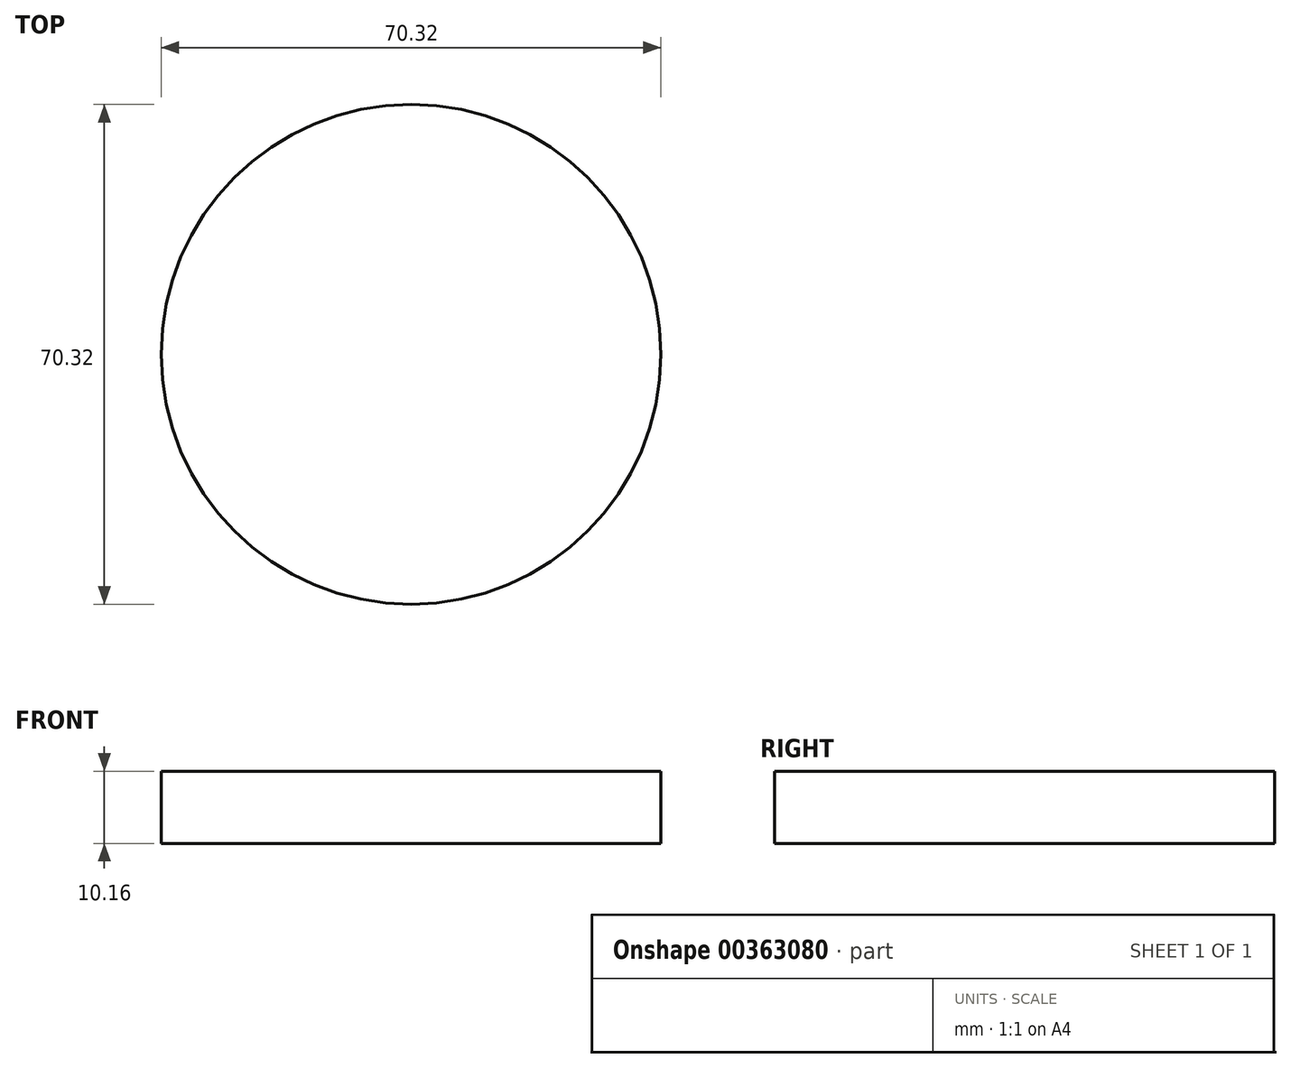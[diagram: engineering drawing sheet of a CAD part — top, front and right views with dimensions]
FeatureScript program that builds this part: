
annotation { "Feature Type Name" : "Feature", "Feature Type Description" : "" }
export const myFeature = defineFeature(function(context is Context, id is Id, definition is map)
    precondition{}
    {
        {
            var Q0;
            Q0=qCreatedBy(makeId("Top.planeOp"),FACE);
            var sketch = newSketch(context, id + "F0", { "sketchPlane" : qUnion([Q0])});
            skCircle(sketch, "E0", {"center": v(0, 0) * mm, "radius": 35.16 * mm});
            skSolve(sketch);
        }
        {
            var Q0;
            Q0=makeQuery(id+"F0.imprint","IMPRINT",FACE,{"disambiguationData":[TD([[makeQuery(id+"F0.imprint","IMPRINT",EDGE,{"derivedFrom":sQuery(id+"F0.wireOp",EDGE,"E0")}),1.0]])]});
            extrude(context, id + "F1", {"entities" : qUnion([Q0]), "depth" : 10.16 * mm});
        }
    });
